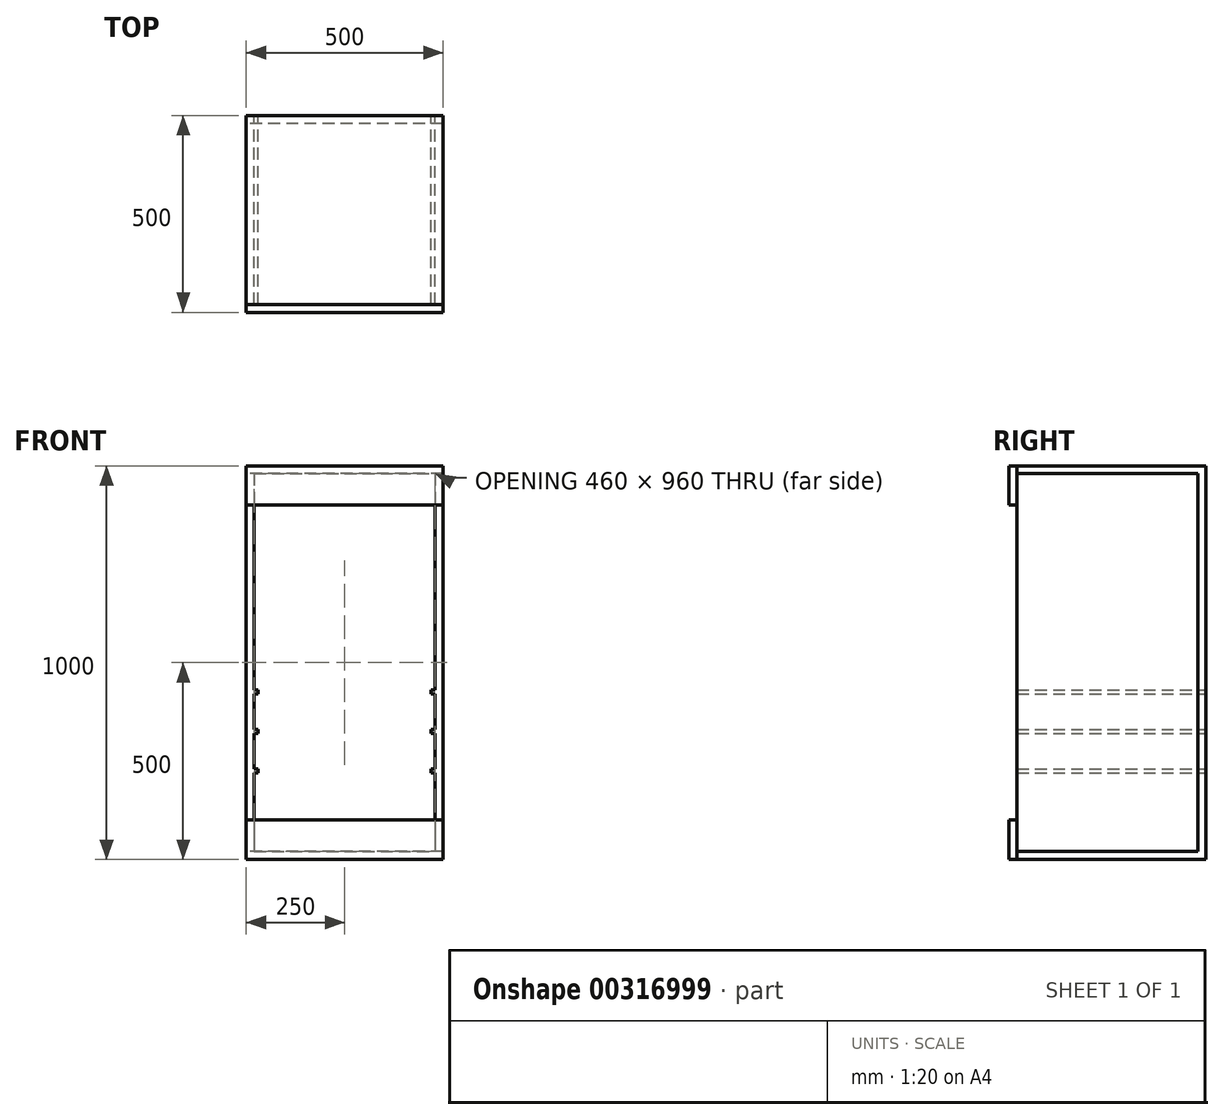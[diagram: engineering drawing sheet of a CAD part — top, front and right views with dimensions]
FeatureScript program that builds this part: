
annotation { "Feature Type Name" : "Feature", "Feature Type Description" : "" }
export const myFeature = defineFeature(function(context is Context, id is Id, definition is map)
    precondition{}
    {
        {
            var Q0;
            Q0=qCreatedBy(makeId("Front.planeOp"),FACE);
            var sketch = newSketch(context, id + "F0", { "sketchPlane" : qUnion([Q0])});
            skLineSegment(sketch, "E0.bottom", {"start": v(-250, 500) * mm, "end": v(250, 500) * mm});
            skLineSegment(sketch, "E0.top", {"start": v(-250, -500) * mm, "end": v(250, -500) * mm});
            skLineSegment(sketch, "E0.left", {"start": v(-250, 500) * mm, "end": v(-250, -500) * mm});
            skLineSegment(sketch, "E0.right", {"start": v(250, 500) * mm, "end": v(250, -500) * mm});
            skPoint(sketch, "E1", {"position": v(-250, 0) * mm});
            skPoint(sketch, "E2", {"position": v(0, 500) * mm});
            skLineSegment(sketch, "E3.bottom", {"start": v(-230, 480) * mm, "end": v(230, 480) * mm});
            skLineSegment(sketch, "E3.top", {"start": v(-230, -480) * mm, "end": v(230, -480) * mm});
            skLineSegment(sketch, "E3.left", {"start": v(-230, 480) * mm, "end": v(-230, -480) * mm});
            skLineSegment(sketch, "E3.right", {"start": v(230, 480) * mm, "end": v(230, -480) * mm});
            skPoint(sketch, "E4", {"position": v(0, 480) * mm});
            skPoint(sketch, "E5", {"position": v(-230, 0) * mm});
            skLineSegment(sketch, "E6.bottom", {"start": v(-230, -280) * mm, "end": v(230, -280) * mm});
            skLineSegment(sketch, "E6.left", {"start": v(-230, -280) * mm, "end": v(-230, -480) * mm});
            skLineSegment(sketch, "E6.right", {"start": v(230, -280) * mm, "end": v(230, -480) * mm});
            skPoint(sketch, "E7", {"position": v(0, -280) * mm});
            skPoint(sketch, "E8", {"position": v(-230, -380) * mm});
            skLineSegment(sketch, "E9.top", {"start": v(-230, 380) * mm, "end": v(230, 380) * mm});
            skLineSegment(sketch, "E9.left", {"start": v(-230, 480) * mm, "end": v(-230, 380) * mm});
            skLineSegment(sketch, "E9.right", {"start": v(230, 480) * mm, "end": v(230, 380) * mm});
            skPoint(sketch, "E10", {"position": v(-230, 430) * mm});
            skLineSegment(sketch, "E11.bottom", {"start": v(-828.37, -40.93) * mm, "end": v(-818.37, -40.93) * mm});
            skLineSegment(sketch, "E11.top", {"start": v(-828.37, -50.93) * mm, "end": v(-818.37, -50.93) * mm});
            skLineSegment(sketch, "E11.left", {"start": v(-828.37, -40.93) * mm, "end": v(-828.37, -50.93) * mm});
            skLineSegment(sketch, "E11.right", {"start": v(-818.37, -40.93) * mm, "end": v(-818.37, -50.93) * mm});
            skLineSegment(sketch, "E12.bottom", {"start": v(-230, -270) * mm, "end": v(-220, -270) * mm});
            skLineSegment(sketch, "E12.top", {"start": v(-230, -280) * mm, "end": v(-220, -280) * mm});
            skLineSegment(sketch, "E12.left", {"start": v(-230, -270) * mm, "end": v(-230, -280) * mm});
            skLineSegment(sketch, "E12.right", {"start": v(-220, -270) * mm, "end": v(-220, -280) * mm});
            skLineSegment(sketch, "E13.bottom", {"start": v(220, -270) * mm, "end": v(230, -270) * mm});
            skLineSegment(sketch, "E13.top", {"start": v(220, -280) * mm, "end": v(230, -280) * mm});
            skLineSegment(sketch, "E13.left", {"start": v(220, -270) * mm, "end": v(220, -280) * mm});
            skLineSegment(sketch, "E13.right", {"start": v(230, -270) * mm, "end": v(230, -280) * mm});
            skPoint(sketch, "E14", {"position": v(230, -180) * mm});
            skLineSegment(sketch, "E15.bottom", {"start": v(220, -170) * mm, "end": v(230, -170) * mm});
            skLineSegment(sketch, "E15.top", {"start": v(220, -180) * mm, "end": v(230, -180) * mm});
            skLineSegment(sketch, "E15.left", {"start": v(220, -170) * mm, "end": v(220, -180) * mm});
            skLineSegment(sketch, "E15.right", {"start": v(230, -170) * mm, "end": v(230, -180) * mm});
            skPoint(sketch, "E16", {"position": v(230, -80) * mm});
            skLineSegment(sketch, "E17.bottom", {"start": v(220, -70) * mm, "end": v(230, -70) * mm});
            skLineSegment(sketch, "E17.top", {"start": v(220, -80) * mm, "end": v(230, -80) * mm});
            skLineSegment(sketch, "E17.left", {"start": v(220, -70) * mm, "end": v(220, -80) * mm});
            skLineSegment(sketch, "E17.right", {"start": v(230, -70) * mm, "end": v(230, -80) * mm});
            skPoint(sketch, "E18", {"position": v(-230, -80) * mm});
            skPoint(sketch, "E19", {"position": v(-230, -180) * mm});
            skLineSegment(sketch, "E20.bottom", {"start": v(-230, -70) * mm, "end": v(-220, -70) * mm});
            skLineSegment(sketch, "E20.top", {"start": v(-230, -80) * mm, "end": v(-220, -80) * mm});
            skLineSegment(sketch, "E20.left", {"start": v(-230, -70) * mm, "end": v(-230, -80) * mm});
            skLineSegment(sketch, "E20.right", {"start": v(-220, -70) * mm, "end": v(-220, -80) * mm});
            skLineSegment(sketch, "E21.bottom", {"start": v(-230, -170) * mm, "end": v(-220, -170) * mm});
            skLineSegment(sketch, "E21.top", {"start": v(-230, -180) * mm, "end": v(-220, -180) * mm});
            skLineSegment(sketch, "E21.left", {"start": v(-230, -170) * mm, "end": v(-230, -180) * mm});
            skLineSegment(sketch, "E21.right", {"start": v(-220, -170) * mm, "end": v(-220, -180) * mm});
            skSolve(sketch);
        }
        {
            var Q0;
            Q0=qCreatedBy(makeId("Right.planeOp"),FACE);
            var sketch = newSketch(context, id + "F1", { "sketchPlane" : qUnion([Q0])});
            skLineSegment(sketch, "E22.bottom", {"start": v(-250, 500) * mm, "end": v(250, 500) * mm});
            skLineSegment(sketch, "E22.top", {"start": v(-250, -500) * mm, "end": v(250, -500) * mm});
            skLineSegment(sketch, "E22.left", {"start": v(-250, 500) * mm, "end": v(-250, -500) * mm});
            skLineSegment(sketch, "E22.right", {"start": v(250, 500) * mm, "end": v(250, -500) * mm});
            skPoint(sketch, "E23", {"position": v(0, 500) * mm});
            skPoint(sketch, "E24", {"position": v(-250, 0) * mm});
            skLineSegment(sketch, "E25.bottom", {"start": v(-230, 480) * mm, "end": v(230, 480) * mm});
            skLineSegment(sketch, "E25.top", {"start": v(-230, -480) * mm, "end": v(230, -480) * mm});
            skLineSegment(sketch, "E25.left", {"start": v(-230, 480) * mm, "end": v(-230, -480) * mm});
            skLineSegment(sketch, "E25.right", {"start": v(230, 480) * mm, "end": v(230, -480) * mm});
            skPoint(sketch, "E26", {"position": v(0, 480) * mm});
            skPoint(sketch, "E27", {"position": v(-230, 0) * mm});
            skLineSegment(sketch, "E28.bottom", {"start": v(-250, 400) * mm, "end": v(-230, 400) * mm});
            skLineSegment(sketch, "E28.top", {"start": v(-250, -400) * mm, "end": v(-230, -400) * mm});
            skLineSegment(sketch, "E28.left", {"start": v(-250, 400) * mm, "end": v(-250, -400) * mm});
            skLineSegment(sketch, "E28.right", {"start": v(-230, 400) * mm, "end": v(-230, -400) * mm});
            skPoint(sketch, "E29", {"position": v(-230, 400) * mm});
            skSolve(sketch);
        }
        {
            var Q0;
            Q0=makeQuery(id+"F0.imprint","IMPRINT",FACE,{"disambiguationData":[TD([[makeQuery(id+"F0.imprint","IMPRINT",EDGE,{"derivedFrom":sQuery(id+"F0.wireOp",EDGE,"E0.bottom")}),-1.0]])]});
            var Q1;
            Q1=makeQuery(id+"F0.imprint","IMPRINT",FACE,{"disambiguationData":[TD([[makeQuery(id+"F0.imprint","IMPRINT",EDGE,{"derivedFrom":sQuery(id+"F0.wireOp",EDGE,"E20.bottom")}),-1.0]])]});
            var Q2;
            Q2=makeQuery(id+"F0.imprint","IMPRINT",FACE,{"disambiguationData":[TD([[makeQuery(id+"F0.imprint","IMPRINT",EDGE,{"derivedFrom":sQuery(id+"F0.wireOp",EDGE,"E21.bottom")}),-1.0]])]});
            var Q3;
            Q3=makeQuery(id+"F0.imprint","IMPRINT",FACE,{"disambiguationData":[TD([[makeQuery(id+"F0.imprint","IMPRINT",EDGE,{"derivedFrom":sQuery(id+"F0.wireOp",EDGE,"E12.bottom")}),-1.0]])]});
            var Q4;
            Q4=makeQuery(id+"F0.imprint","IMPRINT",FACE,{"disambiguationData":[TD([[makeQuery(id+"F0.imprint","IMPRINT",EDGE,{"derivedFrom":sQuery(id+"F0.wireOp",EDGE,"E13.bottom")}),-1.0]])]});
            var Q5;
            Q5=makeQuery(id+"F0.imprint","IMPRINT",FACE,{"disambiguationData":[TD([[makeQuery(id+"F0.imprint","IMPRINT",EDGE,{"derivedFrom":sQuery(id+"F0.wireOp",EDGE,"E15.bottom")}),-1.0]])]});
            var Q6;
            Q6=makeQuery(id+"F0.imprint","IMPRINT",FACE,{"disambiguationData":[TD([[makeQuery(id+"F0.imprint","IMPRINT",EDGE,{"derivedFrom":sQuery(id+"F0.wireOp",EDGE,"E17.bottom")}),-1.0]])]});
            extrude(context, id + "F2", {"entities" : qUnion([Q0, Q1, Q2, Q3, Q4, Q5, Q6]), "depth" : 230 * mm, "hasSecondDirection" : true, "secondDirectionOppositeDirection" : true, "secondDirectionDepth" : 250 * mm});
        }
        {
            var Q0;
            {var subQ6=sQuery(id+"F1.wireOp",EDGE,"E22.bottom");Q0=makeQuery(id+"F1.imprint","IMPRINT",FACE,{"disambiguationData":[TD([[makeQuery(id+"F1.imprint","IMPRINT",EDGE,{"derivedFrom":subQ6}),-1.0]])]});}
            extrude(context, id + "F3", {"entities" : qUnion([Q0]), "depth" : 250 * mm, "hasSecondDirection" : true, "secondDirectionOppositeDirection" : true, "secondDirectionDepth" : 250 * mm});
        }
    });
